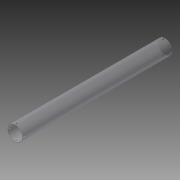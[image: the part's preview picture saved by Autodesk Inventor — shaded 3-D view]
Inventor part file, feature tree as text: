
AUTODESK INVENTOR PART (.ipt)
format: ipt  version: 2014 (Build 180170000, 170)  size: 133,120 bytes
history: native  units: in
note: dims shown in document units (in); Inventor stores cm internally (conversion verified against a paired STEP export)
features: extrude x3, sketch x3, plane x2, projected_geometry x1
ambient origin geometry x8: Origin, YZ Plane, XZ Plane, XY Plane, X Axis, Y Axis, Z Axis, Center Point
bodies: Solid1 (feature_tree)
feature tree (9):
  extrude  "Extrusion1"  Depth=1.875in
  plane  "Work Plane1"
  extrude  "Extrusion2"  Depth=10.004in
  plane  "Work Plane2"
  extrude  "Extrusion3"  Depth=0.2188in
  sketch  "Sketch1"  dims[d0=2.0in d1=1.875in]
  sketch  "Sketch2"  dims[d2=20.008in d3=0.0in d4=10.004in]
  projected_geometry  "Projected Loop1"
  sketch  "Sketch3"  dims[d5=0.19in d6=0.2188in d7=1.0in d8=2.0in d9=0.0in d10=10.004in d11=0.19in d12=0.2188in d13=1.0in d14=2.0in d15=0.0in]
